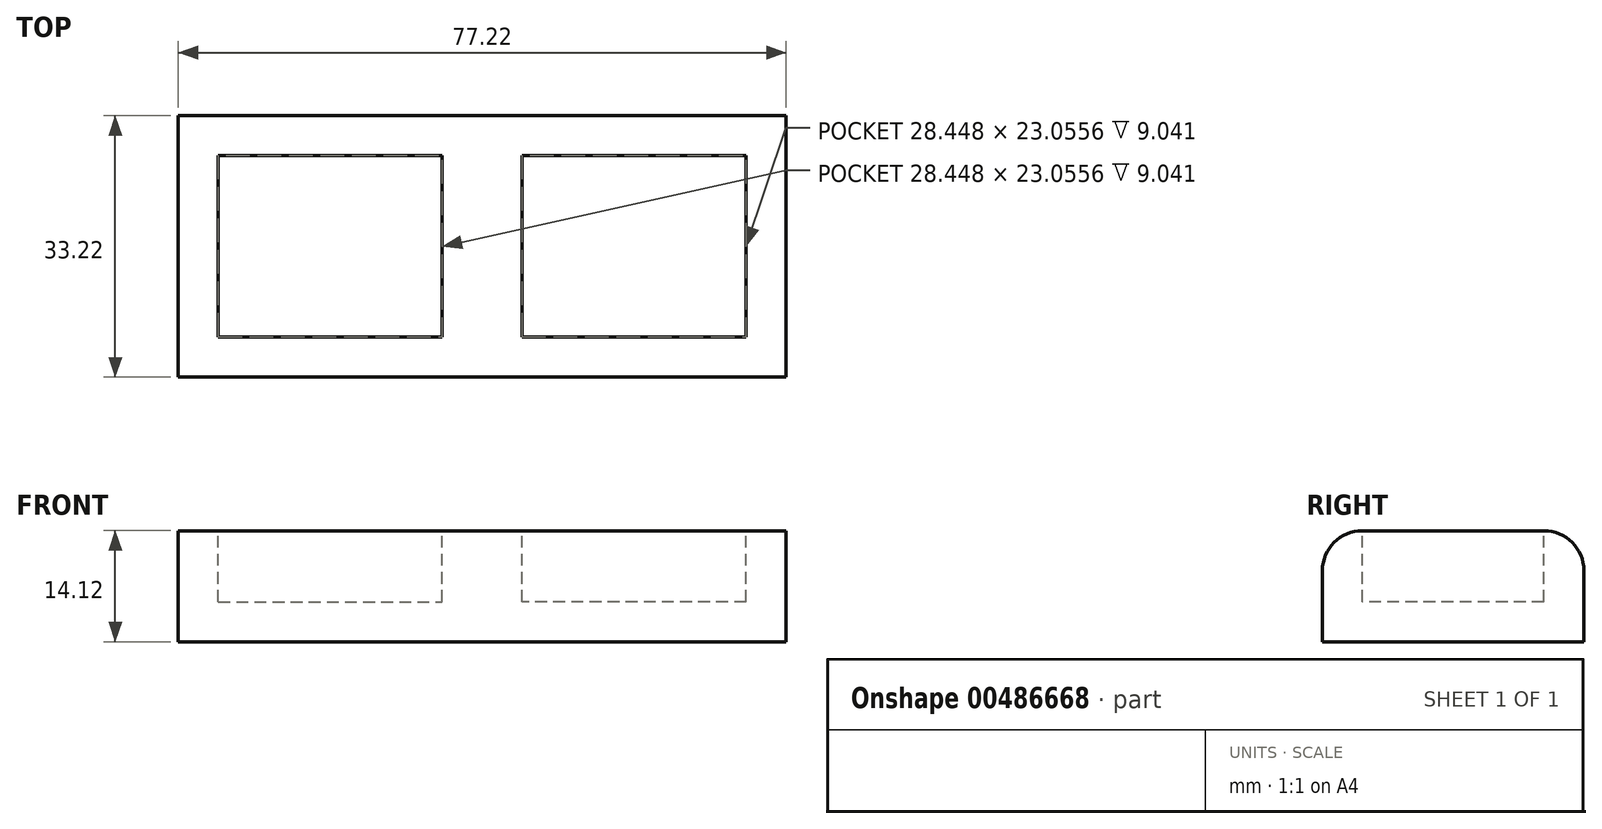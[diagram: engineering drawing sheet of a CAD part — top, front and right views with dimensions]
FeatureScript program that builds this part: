
annotation { "Feature Type Name" : "Feature", "Feature Type Description" : "" }
export const myFeature = defineFeature(function(context is Context, id is Id, definition is map)
    precondition{}
    {
        {
            var Q0;
            Q0=qCreatedBy(makeId("Right.planeOp"),FACE);
            var sketch = newSketch(context, id + "F0", { "sketchPlane" : qUnion([Q0])});
            skLineSegment(sketch, "E0.bottom", {"start": v(-39.5, 21.1) * mm, "end": v(3.91, 21.1) * mm});
            skLineSegment(sketch, "E0.top", {"start": v(-39.5, 14.8) * mm, "end": v(3.91, 14.8) * mm});
            skLineSegment(sketch, "E0.left", {"start": v(-39.5, 21.1) * mm, "end": v(-39.5, 14.8) * mm});
            skLineSegment(sketch, "E0.right", {"start": v(3.91, 21.1) * mm, "end": v(3.91, 14.8) * mm});
            skLineSegment(sketch, "E1.bottom", {"start": v(-39.5, 21.1) * mm, "end": v(-72.72, 21.1) * mm});
            skLineSegment(sketch, "E1.top", {"start": v(-39.5, 35.23) * mm, "end": v(-72.72, 35.23) * mm});
            skLineSegment(sketch, "E1.left", {"start": v(-39.5, 21.1) * mm, "end": v(-39.5, 35.23) * mm});
            skLineSegment(sketch, "E1.right", {"start": v(-72.72, 21.1) * mm, "end": v(-72.72, 35.23) * mm});
            skSolve(sketch);
        }
        {
            var Q0;
            Q0=makeQuery(id+"F0.imprint","IMPRINT",FACE,{"disambiguationData":[TD([[makeQuery(id+"F0.imprint","IMPRINT",EDGE,{"derivedFrom":sQuery(id+"F0.wireOp",EDGE,"E1.bottom")}),-1.0]])]});
            extrude(context, id + "F1", {"entities" : qUnion([Q0]), "depth" : 38.6 * mm});
        }
        {
            var Q0;
            Q0=makeQuery(id+"F1.opExtrude","SWEPT_EDGE",EDGE,{"disambiguationData":[OSD([sQuery(id+"F0.wireOp",EDGE,"E1.top"),sQuery(id+"F0.wireOp",EDGE,"E1.right")])]});
            fillet(context, id + "F2", {"entities" : qUnion([Q0]), "radius" : 5.08 * mm, "tangentPropagation" : true, "allowEdgeOverflow" : false});
        }
        {
            var Q0;
            Q0=makeQuery(id+"F1.opExtrude","SWEPT_EDGE",EDGE,{"disambiguationData":[OSD([sQuery(id+"F0.wireOp",EDGE,"E1.top"),sQuery(id+"F0.wireOp",EDGE,"E1.left")])]});
            fillet(context, id + "F3", {"entities" : qUnion([Q0]), "radius" : 5.08 * mm, "tangentPropagation" : true, "allowEdgeOverflow" : false});
        }
        {
            var Q0;
            Q0=makeQuery(id+"F1.opExtrude","SWEPT_FACE",FACE,{"disambiguationData":[OSD([sQuery(id+"F0.wireOp",EDGE,"E1.top")])]});
            shell(context, id + "F4", {"entities" : qUnion([Q0]), "thickness" : 5.08 * mm});
        }
        {
            var Q0;
            Q0=makeQuery(id+"F1.opExtrude","SWEPT_BODY",BODY,{"disambiguationData":[OSD([sQuery(id+"F0.wireOp",EDGE,"E1.bottom"),sQuery(id+"F0.wireOp",EDGE,"E1.top"),sQuery(id+"F0.wireOp",EDGE,"E1.left"),sQuery(id+"F0.wireOp",EDGE,"E1.right")])]});
            var Q1;
            Q1=qCreatedBy(makeId("Right.planeOp"),FACE);
            mirror(context, id + "F5", {"operationType" : NewBodyOperationType.ADD, "entities" : qUnion([Q0]), "mirrorPlane" : qUnion([Q1])});
        }
    });
